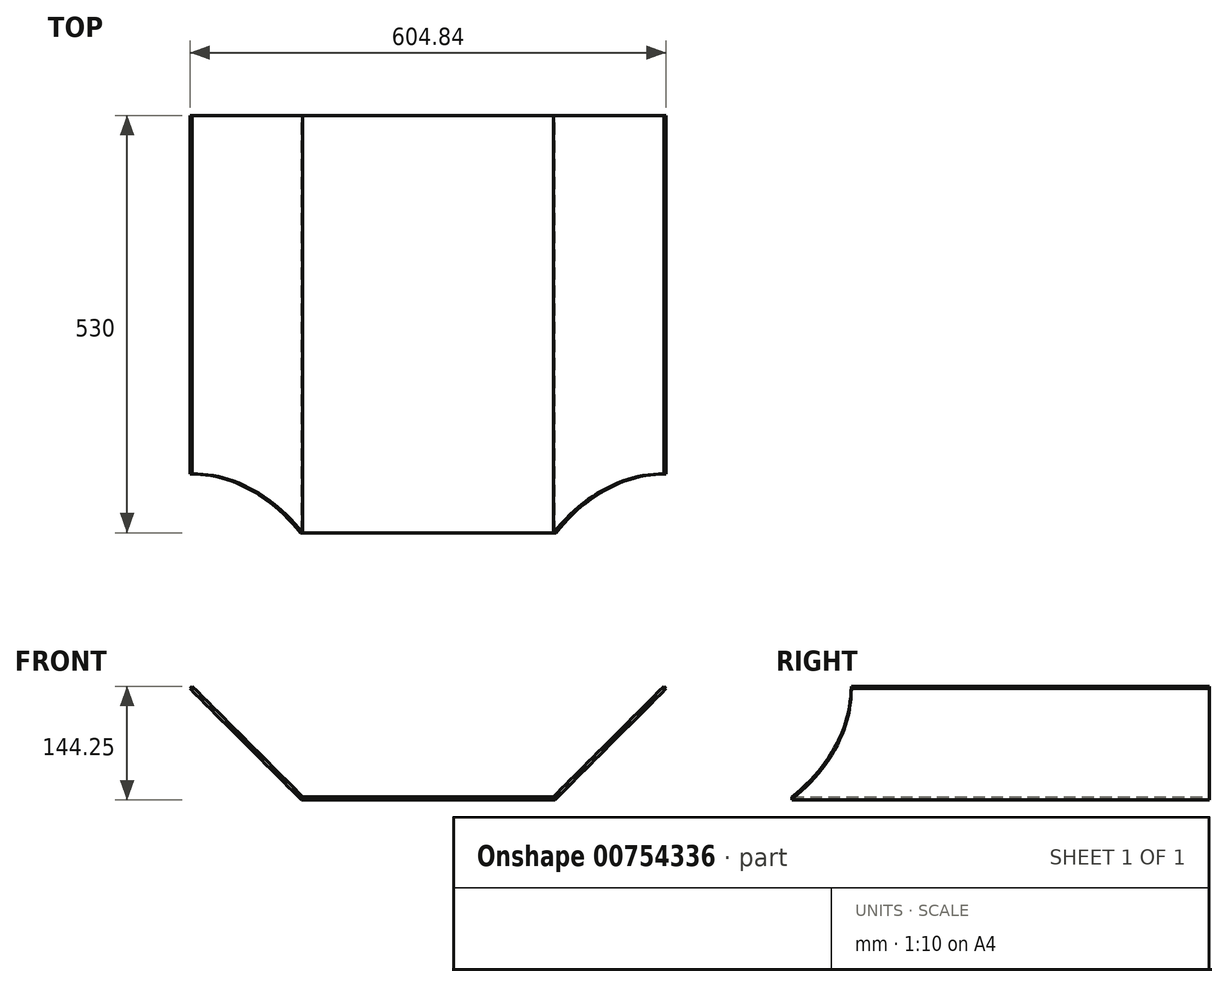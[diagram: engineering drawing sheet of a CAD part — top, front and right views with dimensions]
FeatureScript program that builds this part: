
annotation { "Feature Type Name" : "Feature", "Feature Type Description" : "" }
export const myFeature = defineFeature(function(context is Context, id is Id, definition is map)
    precondition{}
    {
        {
            var Q0;
            Q0=qCreatedBy(makeId("Front.planeOp"),FACE);
            var sketch = newSketch(context, id + "F0", { "sketchPlane" : qUnion([Q0])});
            skLineSegment(sketch, "E0", {"start": v(0, 0) * mm, "end": v(161, 0) * mm});
            skLineSegment(sketch, "E1", {"start": v(161, 0) * mm, "end": v(302.42, 141.42) * mm});
            skLineSegment(sketch, "E2", {"start": v(302.42, 141.42) * mm, "end": v(299.6, 144.25) * mm});
            skLineSegment(sketch, "E3", {"start": v(299.6, 144.25) * mm, "end": v(159.34, 4) * mm});
            skLineSegment(sketch, "E4", {"start": v(159.34, 4) * mm, "end": v(0, 4) * mm});
            skLineSegment(sketch, "E5", {"start": v(0, 4) * mm, "end": v(-159.34, 4) * mm});
            skLineSegment(sketch, "E6", {"start": v(-159.34, 4) * mm, "end": v(-299.6, 144.25) * mm});
            skLineSegment(sketch, "E7", {"start": v(-299.6, 144.25) * mm, "end": v(-302.42, 141.42) * mm});
            skLineSegment(sketch, "E8", {"start": v(-302.42, 141.42) * mm, "end": v(-161, 0) * mm});
            skLineSegment(sketch, "E9", {"start": v(-161, 0) * mm, "end": v(0, 0) * mm});
            skSolve(sketch);
        }
        {
            var Q0;
            Q0=qSketchRegion(id+"F0",true);
            extrude(context, id + "F1", {"entities" : qUnion([Q0]), "depth" : 480 * mm, "offsetDistance" : 25 * mm});
        }
        {
            var Q0;
            Q0=makeQuery(id+"F1.opExtrude","CAP_FACE",FACE,{"disambiguationData":[OSD([sQuery(id+"F0.wireOp",EDGE,"E0"),sQuery(id+"F0.wireOp",EDGE,"E1"),sQuery(id+"F0.wireOp",EDGE,"E2"),sQuery(id+"F0.wireOp",EDGE,"E3"),sQuery(id+"F0.wireOp",EDGE,"E4"),sQuery(id+"F0.wireOp",EDGE,"E5"),sQuery(id+"F0.wireOp",EDGE,"E6"),sQuery(id+"F0.wireOp",EDGE,"E7"),sQuery(id+"F0.wireOp",EDGE,"E8"),sQuery(id+"F0.wireOp",EDGE,"E9")])],"isStart":false});
            var sketch = newSketch(context, id + "F2", { "sketchPlane" : qUnion([Q0])});
            skLineSegment(sketch, "E10", {"start": v(-302.42, 141.42) * mm, "end": v(-299.6, 144.25) * mm});
            skLineSegment(sketch, "E11", {"start": v(-299.6, 144.25) * mm, "end": v(-159.34, 4) * mm});
            skLineSegment(sketch, "E12", {"start": v(-159.34, 4) * mm, "end": v(159.34, 4) * mm});
            skLineSegment(sketch, "E13", {"start": v(159.34, 4) * mm, "end": v(299.6, 144.25) * mm});
            skLineSegment(sketch, "E14", {"start": v(299.6, 144.25) * mm, "end": v(302.42, 141.42) * mm});
            skLineSegment(sketch, "E15", {"start": v(302.42, 141.42) * mm, "end": v(161, 0) * mm});
            skLineSegment(sketch, "E16", {"start": v(161, 0) * mm, "end": v(-161, 0) * mm});
            skLineSegment(sketch, "E17", {"start": v(-161, 0) * mm, "end": v(-302.42, 141.42) * mm});
            skSolve(sketch);
        }
        {
            var Q0;
            Q0 = qSketchRegion(id + "F2", true);
            extrude(context, id + "F3", {"entities" : qUnion([Q0]), "operationType" : NewBodyOperationType.ADD, "depth" : 50 * mm, "offsetDistance" : 25 * mm});
        }
        {
            var Q0;
            Q0=makeQuery(id+"F3.boolean.opBoolean","MERGE",FACE,{"derivedFrom":[makeQuery(id+"F1.opExtrude","SWEPT_FACE",FACE,{"disambiguationData":[OSD([sQuery(id+"F0.wireOp",EDGE,"E6")])]}),makeQuery(id+"F3.opExtrude","SWEPT_FACE",FACE,{"disambiguationData":[OSD([sQuery(id+"F2.wireOp",EDGE,"E11")])]})]});
            var sketch = newSketch(context, id + "F4", { "sketchPlane" : qUnion([Q0])});
            skArc(sketch, "E18", {"start": v(-530, 115.5) * mm, "mid": v(-474.38, 207.82) * mm, "end": v(-455, 313.84) * mm});
            skLineSegment(sketch, "E19", {"start": v(-455, 313.84) * mm, "end": v(-754.77, 313.84) * mm});
            skLineSegment(sketch, "E20", {"start": v(-754.77, 313.84) * mm, "end": v(-530, 115.5) * mm});
            skLineSegment(sketch, "E21", {"start": v(-455, 313.84) * mm, "end": v(-530, 313.84) * mm, "construction": true});
            skSolve(sketch);
        }
        {
            var Q0;
            Q0 = qSketchRegion(id + "F4", true);
            extrude(context, id + "F5", {"entities" : qUnion([Q0]), "operationType" : NewBodyOperationType.REMOVE, "oppositeDirection" : true, "depth" : 25 * mm, "offsetDistance" : 25 * mm});
        }
        {
            var Q0;
            Q0=makeQuery(id+"F3.boolean.opBoolean","MERGE",FACE,{"derivedFrom":[makeQuery(id+"F1.opExtrude","SWEPT_FACE",FACE,{"disambiguationData":[OSD([sQuery(id+"F0.wireOp",EDGE,"E3")])]}),makeQuery(id+"F3.opExtrude","SWEPT_FACE",FACE,{"disambiguationData":[OSD([sQuery(id+"F2.wireOp",EDGE,"E13")])]})]});
            var sketch = newSketch(context, id + "F6", { "sketchPlane" : qUnion([Q0])});
            skArc(sketch, "E22", {"start": v(455, 313.84) * mm, "mid": v(474.38, 207.82) * mm, "end": v(530, 115.5) * mm});
            skLineSegment(sketch, "E23", {"start": v(455, 313.84) * mm, "end": v(530, 313.84) * mm, "construction": true});
            skLineSegment(sketch, "E24", {"start": v(530, 115.5) * mm, "end": v(754.77, 313.84) * mm});
            skLineSegment(sketch, "E25", {"start": v(455, 313.84) * mm, "end": v(754.77, 313.84) * mm});
            skSolve(sketch);
        }
        {
            var Q0;
            Q0 = qSketchRegion(id + "F6", true);
            extrude(context, id + "F7", {"entities" : qUnion([Q0]), "operationType" : NewBodyOperationType.REMOVE, "oppositeDirection" : true, "depth" : 25 * mm, "offsetDistance" : 25 * mm});
        }
    });
